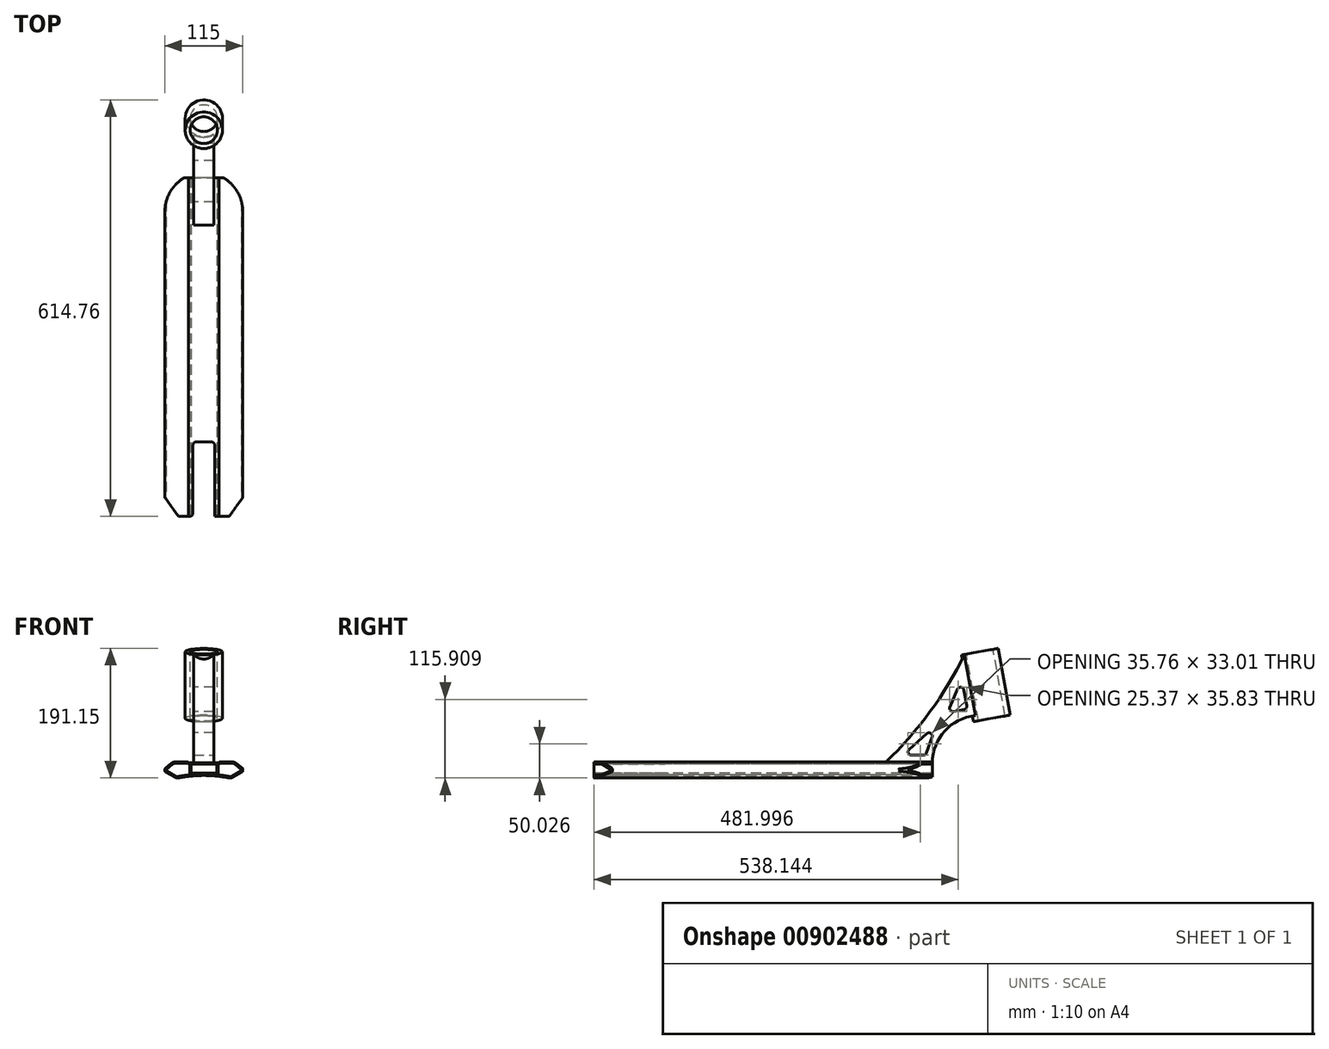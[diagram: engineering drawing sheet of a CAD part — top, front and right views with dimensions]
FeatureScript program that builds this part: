
annotation { "Feature Type Name" : "Feature", "Feature Type Description" : "" }
export const myFeature = defineFeature(function(context is Context, id is Id, definition is map)
    precondition{}
    {
        {
            var Q0;
            Q0=qCreatedBy(makeId("Front.planeOp"),FACE);
            var sketch = newSketch(context, id + "F0", { "sketchPlane" : qUnion([Q0])});
            skLineSegment(sketch, "E0", {"start": v(0, 0) * mm, "end": v(0, 87.82) * mm, "construction": true});
            skLineSegment(sketch, "E1", {"start": v(0, 8.7) * mm, "end": v(-22.5, 8.7) * mm});
            skLineSegment(sketch, "E2", {"start": v(-22.5, 8.7) * mm, "end": v(-22.5, 10) * mm});
            skLineSegment(sketch, "E3", {"start": v(-22.5, 10) * mm, "end": v(-45.58, 10) * mm});
            skLineSegment(sketch, "E4", {"start": v(-45.58, 10) * mm, "end": v(-57.5, 0) * mm});
            skLineSegment(sketch, "E5", {"start": v(-57.5, 0) * mm, "end": v(-57.5, -4) * mm});
            skLineSegment(sketch, "E6", {"start": v(-57.5, -4) * mm, "end": v(-40.18, -14) * mm});
            skLineSegment(sketch, "E7.MirrorCS", {"start": v(22.5, 8.7) * mm, "end": v(22.5, 10) * mm});
            skLineSegment(sketch, "E8.MirrorCS", {"start": v(57.5, 0) * mm, "end": v(57.5, -4) * mm});
            skLineSegment(sketch, "E9.MirrorCS", {"start": v(57.5, -4) * mm, "end": v(40.18, -14) * mm});
            skLineSegment(sketch, "E10.MirrorCS", {"start": v(0, 8.7) * mm, "end": v(22.5, 8.7) * mm});
            skLineSegment(sketch, "E11.MirrorCS", {"start": v(45.58, 10) * mm, "end": v(57.5, 0) * mm});
            skLineSegment(sketch, "E12.MirrorCS", {"start": v(22.5, 10) * mm, "end": v(45.58, 10) * mm});
            skArc(sketch, "E13", {"start": v(40.18, -14) * mm, "mid": v(0, -9.92) * mm, "end": v(-40.18, -14) * mm});
            skSolve(sketch);
        }
        {
            var Q0;
            Q0=makeQuery(id+"F0.imprint","IMPRINT",FACE,{"disambiguationData":[TD([[makeQuery(id+"F0.imprint","IMPRINT",EDGE,{"derivedFrom":sQuery(id+"F0.wireOp",EDGE,"E1")}),1.0]])]});
            extrude(context, id + "F1", {"entities" : qUnion([Q0]), "endBound" : BoundingType.SYMMETRIC, "depth" : 500 * mm, "offsetDistance" : 25 * mm});
        }
        {
            var Q0;
            Q0=qCreatedBy(makeId("Front.planeOp"),FACE);
            var sketch = newSketch(context, id + "F2", { "sketchPlane" : qUnion([Q0])});
            skLineSegment(sketch, "E14.bottom", {"start": v(-19, 6.7) * mm, "end": v(19, 6.7) * mm});
            skLineSegment(sketch, "E14.top", {"start": v(-19, -6.3) * mm, "end": v(19, -6.3) * mm});
            skLineSegment(sketch, "E14.left", {"start": v(-19, 6.7) * mm, "end": v(-19, -6.3) * mm});
            skLineSegment(sketch, "E14.right", {"start": v(19, 6.7) * mm, "end": v(19, -6.3) * mm});
            skSolve(sketch);
        }
        {
            var Q0;
            Q0 = qSketchRegion(id + "F2", true);
            extrude(context, id + "F3", {"entities" : qUnion([Q0]), "operationType" : NewBodyOperationType.REMOVE, "endBound" : BoundingType.SYMMETRIC, "oppositeDirection" : true, "depth" : 500 * mm, "offsetDistance" : 25 * mm});
        }
        {
            var Q0;
            Q0=makeQuery(id+"F1.opExtrude","SWEPT_EDGE",EDGE,{"disambiguationData":[OSD([sQuery(id+"F0.wireOp",EDGE,"E2"),sQuery(id+"F0.wireOp",EDGE,"E3")])]});
            var Q1;
            Q1=makeQuery(id+"F1.opExtrude","SWEPT_EDGE",EDGE,{"disambiguationData":[OSD([sQuery(id+"F0.wireOp",EDGE,"E7.MirrorCS"),sQuery(id+"F0.wireOp",EDGE,"E12.MirrorCS")])]});
            fillet(context, id + "F4", {"entities" : qUnion([Q0, Q1]), "radius" : 2 * mm, "tangentPropagation" : true, "allowEdgeOverflow" : false});
        }
        {
            var Q0;
            Q0=makeQuery(id+"F1.opExtrude","SWEPT_EDGE",EDGE,{"disambiguationData":[OSD([sQuery(id+"F0.wireOp",EDGE,"E3"),sQuery(id+"F0.wireOp",EDGE,"E4")])]});
            var Q1;
            Q1=makeQuery(id+"F1.opExtrude","SWEPT_EDGE",EDGE,{"disambiguationData":[OSD([sQuery(id+"F0.wireOp",EDGE,"E11.MirrorCS"),sQuery(id+"F0.wireOp",EDGE,"E12.MirrorCS")])]});
            var Q2;
            Q2=makeQuery(id+"F1.opExtrude","SWEPT_EDGE",EDGE,{"disambiguationData":[OSD([sQuery(id+"F0.wireOp",EDGE,"E6"),sQuery(id+"F0.wireOp",EDGE,"E13")])]});
            var Q3;
            Q3=makeQuery(id+"F1.opExtrude","SWEPT_EDGE",EDGE,{"disambiguationData":[OSD([sQuery(id+"F0.wireOp",EDGE,"E9.MirrorCS"),sQuery(id+"F0.wireOp",EDGE,"E13")])]});
            fillet(context, id + "F5", {"entities" : qUnion([Q0, Q1, Q2, Q3]), "radius" : 9 * mm, "tangentPropagation" : true, "allowEdgeOverflow" : false});
        }
        {
            var Q0;
            Q0=makeQuery(id+"F1.opExtrude","SWEPT_EDGE",EDGE,{"disambiguationData":[OSD([sQuery(id+"F0.wireOp",EDGE,"E4"),sQuery(id+"F0.wireOp",EDGE,"E5")])]});
            var Q1;
            Q1=makeQuery(id+"F1.opExtrude","SWEPT_EDGE",EDGE,{"disambiguationData":[OSD([sQuery(id+"F0.wireOp",EDGE,"E5"),sQuery(id+"F0.wireOp",EDGE,"E6")])]});
            var Q2;
            Q2=makeQuery(id+"F1.opExtrude","SWEPT_EDGE",EDGE,{"disambiguationData":[OSD([sQuery(id+"F0.wireOp",EDGE,"E8.MirrorCS"),sQuery(id+"F0.wireOp",EDGE,"E11.MirrorCS")])]});
            var Q3;
            Q3=makeQuery(id+"F1.opExtrude","SWEPT_EDGE",EDGE,{"disambiguationData":[OSD([sQuery(id+"F0.wireOp",EDGE,"E8.MirrorCS"),sQuery(id+"F0.wireOp",EDGE,"E9.MirrorCS")])]});
            fillet(context, id + "F6", {"entities" : qUnion([Q0, Q1, Q2, Q3]), "radius" : 1 * mm, "tangentPropagation" : true, "allowEdgeOverflow" : false});
        }
        {
            var Q0;
            Q0=makeQuery(id+"F1.opExtrude","CAP_FACE",FACE,{"disambiguationData":[OSD([sQuery(id+"F0.wireOp",EDGE,"E1"),sQuery(id+"F0.wireOp",EDGE,"E2"),sQuery(id+"F0.wireOp",EDGE,"E3"),sQuery(id+"F0.wireOp",EDGE,"E4"),sQuery(id+"F0.wireOp",EDGE,"E5"),sQuery(id+"F0.wireOp",EDGE,"E6"),sQuery(id+"F0.wireOp",EDGE,"E7.MirrorCS"),sQuery(id+"F0.wireOp",EDGE,"E8.MirrorCS"),sQuery(id+"F0.wireOp",EDGE,"E9.MirrorCS"),sQuery(id+"F0.wireOp",EDGE,"E10.MirrorCS"),sQuery(id+"F0.wireOp",EDGE,"E11.MirrorCS"),sQuery(id+"F0.wireOp",EDGE,"E12.MirrorCS"),sQuery(id+"F0.wireOp",EDGE,"E13")])],"isStart":false});
            var sketch = newSketch(context, id + "F7", { "sketchPlane" : qUnion([Q0])});
            skLineSegment(sketch, "E15.0", {"start": v(-24.37, 8) * mm, "end": v(-42.3, 8) * mm});
            skLineSegment(sketch, "E16.0", {"start": v(-46.8, 6.36) * mm, "end": v(-55.14, -0.63) * mm});
            skArc(sketch, "E17.0", {"start": v(-42.3, 8) * mm, "mid": v(-44.7, 7.58) * mm, "end": v(-46.8, 6.36) * mm});
            skLineSegment(sketch, "E18.0", {"start": v(-55, -3.13) * mm, "end": v(-42.1, -10.58) * mm});
            skArc(sketch, "E19.0", {"start": v(-42.1, -10.58) * mm, "mid": v(-39.78, -11.42) * mm, "end": v(-37.3, -11.4) * mm});
            skLineSegment(sketch, "E20.0", {"start": v(-55.5, -1.4) * mm, "end": v(-55.5, -2.27) * mm});
            skLineSegment(sketch, "E21.0", {"start": v(-24.37, 8) * mm, "end": v(-24.37, 8) * mm});
            skArc(sketch, "E22.0", {"start": v(-21, -9.02) * mm, "mid": v(-29.18, -10.04) * mm, "end": v(-37.3, -11.4) * mm});
            skPoint(sketch, "E23.visualSharp", {"position": v(-55.5, -2.85) * mm});
            skArc(sketch, "E23.filletArc", {"start": v(-55.5, -2.27) * mm, "mid": v(-55.37, -2.77) * mm, "end": v(-55, -3.13) * mm});
            skPoint(sketch, "E24.visualSharp", {"position": v(-55.5, -0.93) * mm});
            skArc(sketch, "E24.filletArc", {"start": v(-55.14, -0.63) * mm, "mid": v(-55.4, -0.98) * mm, "end": v(-55.5, -1.4) * mm});
            skLineSegment(sketch, "E25.0", {"start": v(-21, 6.7) * mm, "end": v(-21, -9.02) * mm});
            skLineSegment(sketch, "E26.0", {"start": v(-22.5, 6.7) * mm, "end": v(-21, 6.7) * mm});
            skArc(sketch, "E27", {"start": v(-22.5, 6.7) * mm, "mid": v(-23.23, 7.64) * mm, "end": v(-24.37, 8) * mm});
            skArc(sketch, "E28.MirrorCS", {"start": v(55.5, -2.27) * mm, "mid": v(55.37, -2.77) * mm, "end": v(55, -3.13) * mm});
            skLineSegment(sketch, "E29.MirrorCS", {"start": v(55.5, -1.4) * mm, "end": v(55.5, -2.27) * mm});
            skArc(sketch, "E30.MirrorCS", {"start": v(55.14, -0.63) * mm, "mid": v(55.4, -0.98) * mm, "end": v(55.5, -1.4) * mm});
            skArc(sketch, "E31.MirrorCS", {"start": v(22.5, 6.7) * mm, "mid": v(23.23, 7.64) * mm, "end": v(24.37, 8) * mm});
            skLineSegment(sketch, "E32.MirrorCS", {"start": v(22.5, 6.7) * mm, "end": v(21, 6.7) * mm});
            skLineSegment(sketch, "E33.MirrorCS", {"start": v(24.37, 8) * mm, "end": v(42.3, 8) * mm});
            skLineSegment(sketch, "E34.MirrorCS", {"start": v(46.8, 6.36) * mm, "end": v(55.14, -0.63) * mm});
            skPoint(sketch, "E35.MirrorP", {"position": v(55.5, -0.93) * mm});
            skArc(sketch, "E36.MirrorCS", {"start": v(42.3, 8) * mm, "mid": v(44.7, 7.58) * mm, "end": v(46.8, 6.36) * mm});
            skLineSegment(sketch, "E37.MirrorCS", {"start": v(24.37, 8) * mm, "end": v(24.37, 8) * mm});
            skPoint(sketch, "E38.MirrorP", {"position": v(55.5, -2.85) * mm});
            skLineSegment(sketch, "E39.MirrorCS", {"start": v(21, 6.7) * mm, "end": v(21, -9.02) * mm});
            skArc(sketch, "E40.MirrorCS", {"start": v(42.1, -10.58) * mm, "mid": v(39.78, -11.42) * mm, "end": v(37.3, -11.4) * mm});
            skArc(sketch, "E41.MirrorCS", {"start": v(21, -9.02) * mm, "mid": v(29.18, -10.04) * mm, "end": v(37.3, -11.4) * mm});
            skLineSegment(sketch, "E42.MirrorCS", {"start": v(55, -3.13) * mm, "end": v(42.1, -10.58) * mm});
            skSolve(sketch);
        }
        {
            var Q0;
            Q0 = qSketchRegion(id + "F7", true);
            extrude(context, id + "F8", {"entities" : qUnion([Q0]), "operationType" : NewBodyOperationType.REMOVE, "endBound" : BoundingType.THROUGH_ALL, "oppositeDirection" : true, "depth" : 25 * mm, "offsetDistance" : 25 * mm});
        }
        {
            var Q0;
            Q0=qCreatedBy(makeId("Top.planeOp"),FACE);
            var sketch = newSketch(context, id + "F9", { "sketchPlane" : qUnion([Q0])});
            skArc(sketch, "E43", {"start": v(57.5, 200) * mm, "mid": v(0, 257.5) * mm, "end": v(-57.5, 200) * mm});
            skLineSegment(sketch, "E44", {"start": v(-57.5, 200) * mm, "end": v(-57.5, 280) * mm});
            skLineSegment(sketch, "E45", {"start": v(57.5, 200) * mm, "end": v(57.5, 280) * mm});
            skLineSegment(sketch, "E46", {"start": v(57.5, 280) * mm, "end": v(-57.5, 280) * mm});
            skSolve(sketch);
        }
        {
            var Q0;
            Q0 = qSketchRegion(id + "F9", true);
            extrude(context, id + "F10", {"entities" : qUnion([Q0]), "operationType" : NewBodyOperationType.REMOVE, "endBound" : BoundingType.THROUGH_ALL, "oppositeDirection" : true, "depth" : 25 * mm, "offsetDistance" : 25 * mm, "hasSecondDirection" : true, "secondDirectionBound" : SecondDirectionBoundingType.THROUGH_ALL, "secondDirectionOppositeDirection" : false, "secondDirectionDepth" : 25 * mm});
        }
        {
            var Q0;
            Q0=qCreatedBy(makeId("Top.planeOp"),FACE);
            var sketch = newSketch(context, id + "F11", { "sketchPlane" : qUnion([Q0])});
            skLineSegment(sketch, "E47", {"start": v(16, -140) * mm, "end": v(-16, -140) * mm});
            skLineSegment(sketch, "E48", {"start": v(-16, -140) * mm, "end": v(-16, -250) * mm});
            skLineSegment(sketch, "E49", {"start": v(-16, -250) * mm, "end": v(-37.49, -250) * mm});
            skLineSegment(sketch, "E50", {"start": v(-37.49, -250) * mm, "end": v(-68, -208) * mm});
            skLineSegment(sketch, "E51", {"start": v(-68, -208) * mm, "end": v(-68, -338) * mm});
            skLineSegment(sketch, "E52", {"start": v(-68, -338) * mm, "end": v(68, -338) * mm});
            skLineSegment(sketch, "E53", {"start": v(68, -338) * mm, "end": v(68, -208) * mm});
            skLineSegment(sketch, "E54", {"start": v(68, -208) * mm, "end": v(37.49, -250) * mm});
            skLineSegment(sketch, "E55", {"start": v(37.49, -250) * mm, "end": v(16, -250) * mm});
            skLineSegment(sketch, "E56", {"start": v(16, -250) * mm, "end": v(16, -140) * mm});
            skSolve(sketch);
        }
        {
            var Q0;
            Q0 = qSketchRegion(id + "F11", true);
            extrude(context, id + "F12", {"entities" : qUnion([Q0]), "operationType" : NewBodyOperationType.REMOVE, "endBound" : BoundingType.THROUGH_ALL, "oppositeDirection" : true, "depth" : 25 * mm, "offsetDistance" : 25 * mm, "hasSecondDirection" : true, "secondDirectionBound" : SecondDirectionBoundingType.THROUGH_ALL, "secondDirectionOppositeDirection" : false, "secondDirectionDepth" : 25 * mm});
        }
        {
            var Q0;
            {var subQ0=sQuery(id+"F11.wireOp",EDGE,"E48");var subQ1=sQuery(id+"F11.wireOp",EDGE,"E47");Q0=makeQuery(id+"F12.boolean.opBoolean","COPY",EDGE,{"disambiguationData":[TD([makeQuery(id+"F3.boolean.opBoolean","COPY",FACE,{"derivedFrom":makeQuery(id+"F3.opExtrude","SWEPT_FACE",FACE,{"disambiguationData":[OSD([sQuery(id+"F2.wireOp",EDGE,"E14.bottom")])]})})])],"derivedFrom":makeQuery(id+"F12.opExtrude","SWEPT_EDGE",EDGE,{"disambiguationData":[OSD([subQ1,subQ0])]})});}
            var Q1;
            {var subQ0=sQuery(id+"F11.wireOp",EDGE,"E47");var subQ1=sQuery(id+"F11.wireOp",EDGE,"E48");Q1=makeQuery(id+"F12.boolean.opBoolean","COPY",EDGE,{"disambiguationData":[TD([makeQuery(id+"F1.opExtrude","SWEPT_FACE",FACE,{"disambiguationData":[OSD([sQuery(id+"F0.wireOp",EDGE,"E13")])]})])],"derivedFrom":makeQuery(id+"F12.opExtrude","SWEPT_EDGE",EDGE,{"disambiguationData":[OSD([subQ0,subQ1])]})});}
            var Q2;
            {var subQ2=sQuery(id+"F11.wireOp",EDGE,"E48");Q2=makeQuery(id+"F12.boolean.opBoolean","COPY",EDGE,{"disambiguationData":[TD([makeQuery(id+"F3.boolean.opBoolean","COPY",FACE,{"derivedFrom":makeQuery(id+"F3.opExtrude","SWEPT_FACE",FACE,{"disambiguationData":[OSD([sQuery(id+"F2.wireOp",EDGE,"E14.bottom")])]})})])],"derivedFrom":makeQuery(id+"F12.opExtrude","SWEPT_EDGE",EDGE,{"disambiguationData":[OSD([subQ2,sQuery(id+"F11.wireOp",EDGE,"E49")])]})});}
            var Q3;
            {var subQ0=sQuery(id+"F0.wireOp",EDGE,"E13");var subQ1=sQuery(id+"F11.wireOp",EDGE,"E48");Q3=makeQuery(id+"F12.boolean.opBoolean","COPY",EDGE,{"disambiguationData":[TD([makeQuery(id+"F1.opExtrude","SWEPT_FACE",FACE,{"disambiguationData":[OSD([subQ0])]})])],"derivedFrom":makeQuery(id+"F12.opExtrude","SWEPT_EDGE",EDGE,{"disambiguationData":[OSD([subQ1,sQuery(id+"F11.wireOp",EDGE,"E49")])]})});}
            var Q4;
            {var subQ0=sQuery(id+"F11.wireOp",EDGE,"E47");var subQ1=sQuery(id+"F11.wireOp",EDGE,"E56");Q4=makeQuery(id+"F12.boolean.opBoolean","COPY",EDGE,{"disambiguationData":[TD([makeQuery(id+"F3.boolean.opBoolean","COPY",FACE,{"derivedFrom":makeQuery(id+"F3.opExtrude","SWEPT_FACE",FACE,{"disambiguationData":[OSD([sQuery(id+"F2.wireOp",EDGE,"E14.bottom")])]})})])],"derivedFrom":makeQuery(id+"F12.opExtrude","SWEPT_EDGE",EDGE,{"disambiguationData":[OSD([subQ0,subQ1])]})});}
            var Q5;
            {var subQ0=sQuery(id+"F11.wireOp",EDGE,"E56");var subQ1=sQuery(id+"F11.wireOp",EDGE,"E47");Q5=makeQuery(id+"F12.boolean.opBoolean","COPY",EDGE,{"disambiguationData":[TD([makeQuery(id+"F1.opExtrude","SWEPT_FACE",FACE,{"disambiguationData":[OSD([sQuery(id+"F0.wireOp",EDGE,"E13")])]})])],"derivedFrom":makeQuery(id+"F12.opExtrude","SWEPT_EDGE",EDGE,{"disambiguationData":[OSD([subQ1,subQ0])]})});}
            var Q6;
            {var subQ2=sQuery(id+"F11.wireOp",EDGE,"E56");Q6=makeQuery(id+"F12.boolean.opBoolean","COPY",EDGE,{"disambiguationData":[TD([makeQuery(id+"F3.boolean.opBoolean","COPY",FACE,{"derivedFrom":makeQuery(id+"F3.opExtrude","SWEPT_FACE",FACE,{"disambiguationData":[OSD([sQuery(id+"F2.wireOp",EDGE,"E14.bottom")])]})})])],"derivedFrom":makeQuery(id+"F12.opExtrude","SWEPT_EDGE",EDGE,{"disambiguationData":[OSD([sQuery(id+"F11.wireOp",EDGE,"E55"),subQ2])]})});}
            var Q7;
            {var subQ0=sQuery(id+"F0.wireOp",EDGE,"E13");var subQ1=sQuery(id+"F11.wireOp",EDGE,"E56");Q7=makeQuery(id+"F12.boolean.opBoolean","COPY",EDGE,{"disambiguationData":[TD([makeQuery(id+"F1.opExtrude","SWEPT_FACE",FACE,{"disambiguationData":[OSD([subQ0])]})])],"derivedFrom":makeQuery(id+"F12.opExtrude","SWEPT_EDGE",EDGE,{"disambiguationData":[OSD([sQuery(id+"F11.wireOp",EDGE,"E55"),subQ1])]})});}
            fillet(context, id + "F13", {"entities" : qUnion([Q0, Q1, Q2, Q3, Q4, Q5, Q6, Q7]), "radius" : 5 * mm, "tangentPropagation" : true, "allowEdgeOverflow" : false});
        }
        {
            var Q0;
            Q0=qCreatedBy(makeId("Right.planeOp"),FACE);
            var sketch = newSketch(context, id + "F14", { "sketchPlane" : qUnion([Q0])});
            skLineSegment(sketch, "E57", {"start": v(180, 8.7) * mm, "end": v(250, 8.7) * mm});
            skArc(sketch, "E58", {"start": v(313.6, 78.4) * mm, "mid": v(268.29, 55.88) * mm, "end": v(250, 8.7) * mm});
            skLineSegment(sketch, "E59", {"start": v(313.6, 78.4) * mm, "end": v(315.06, 70.27) * mm});
            skLineSegment(sketch, "E60", {"start": v(315.06, 70.27) * mm, "end": v(360.34, 78.4) * mm});
            skLineSegment(sketch, "E61", {"start": v(360.34, 78.4) * mm, "end": v(342.66, 176.83) * mm});
            skLineSegment(sketch, "E62", {"start": v(342.66, 176.83) * mm, "end": v(297.38, 168.7) * mm});
            skArc(sketch, "E63", {"start": v(180, 8.7) * mm, "mid": v(245.97, 83.36) * mm, "end": v(297.38, 168.7) * mm});
            skSolve(sketch);
        }
        {
            var Q0;
            Q0 = qSketchRegion(id + "F14", true);
            extrude(context, id + "F15", {"entities" : qUnion([Q0]), "endBound" : BoundingType.SYMMETRIC, "depth" : 30 * mm, "offsetDistance" : 25 * mm});
        }
        {
            var Q0;
            Q0=makeQuery(id+"F15.opExtrude","SWEPT_FACE",FACE,{"disambiguationData":[OSD([sQuery(id+"F14.wireOp",EDGE,"E62")])]});
            var sketch = newSketch(context, id + "F16", { "sketchPlane" : qUnion([Q0])});
            skCircle(sketch, "E64", {"center": v(0, 345.52) * mm, "radius": 27.5 * mm});
            skSolve(sketch);
        }
        {
            var Q0;
            Q0 = qSketchRegion(id + "F16", true);
            var Q1;
            Q1=makeQuery(id+"F15.opExtrude","SWEPT_FACE",FACE,{"disambiguationData":[OSD([sQuery(id+"F14.wireOp",EDGE,"E60")])]});
            extrude(context, id + "F17", {"entities" : qUnion([Q0]), "operationType" : NewBodyOperationType.ADD, "endBound" : BoundingType.UP_TO_SURFACE, "oppositeDirection" : true, "depth" : 25 * mm, "endBoundEntityFace" : qUnion([Q1]), "offsetDistance" : 25 * mm});
        }
        {
            var Q0;
            Q0=makeQuery(id+"F17.boolean.opBoolean","MERGE",FACE,{"derivedFrom":[makeQuery(id+"F15.opExtrude","SWEPT_FACE",FACE,{"disambiguationData":[OSD([sQuery(id+"F14.wireOp",EDGE,"E62")])]}),makeQuery(id+"F17.opExtrude","CAP_FACE",FACE,{"disambiguationData":[OSD([sQuery(id+"F16.wireOp",EDGE,"E64")])],"isStart":true})]});
            var sketch = newSketch(context, id + "F18", { "sketchPlane" : qUnion([Q0])});
            skPoint(sketch, "E65", {"position": v(0, 345.52) * mm});
            skSolve(sketch);
        }
        {
            var Q0;
            Q0=sQuery(id+"F18.wireOp",VERTEX,"E65");
            var Q1;
            Q1=makeQuery(id+"F15.opExtrude","SWEPT_BODY",BODY,{"disambiguationData":[OSD([sQuery(id+"F14.wireOp",EDGE,"E57"),sQuery(id+"F14.wireOp",EDGE,"E58"),sQuery(id+"F14.wireOp",EDGE,"E59"),sQuery(id+"F14.wireOp",EDGE,"E60"),sQuery(id+"F14.wireOp",EDGE,"E61"),sQuery(id+"F14.wireOp",EDGE,"E62"),sQuery(id+"F14.wireOp",EDGE,"E63")])]});
            hole(context, id + "F19", {"style" : HoleStyle.SIMPLE, "endStyle" : HoleEndStyle.THROUGH, "holeDiameter" : 40 * mm, "majorDiameter" : 5 * mm, "isTappedThrough" : true, "tappedDepth" : 12 * mm, "tapClearance" : 3, "locations" : qUnion([Q0]), "scope" : qUnion([Q1])});
        }
        {
            var Q0;
            Q0=makeQuery(id+"F8.boolean.opBoolean","COPY",FACE,{"derivedFrom":makeQuery(id+"F8.opExtrude","SWEPT_FACE",FACE,{"disambiguationData":[OSD([sQuery(id+"F7.wireOp",EDGE,"E39.MirrorCS")])]})});
            var sketch = newSketch(context, id + "F20", { "sketchPlane" : qUnion([Q0])});
            skPoint(sketch, "E66", {"position": v(-236, 0.98) * mm});
            skSolve(sketch);
        }
        {
            var Q0;
            Q0=sQuery(id+"F20.wireOp",VERTEX,"E66");
            var Q1;
            Q1=makeQuery(id+"F15.opExtrude","SWEPT_BODY",BODY,{"disambiguationData":[OSD([sQuery(id+"F14.wireOp",EDGE,"E57"),sQuery(id+"F14.wireOp",EDGE,"E58"),sQuery(id+"F14.wireOp",EDGE,"E59"),sQuery(id+"F14.wireOp",EDGE,"E60"),sQuery(id+"F14.wireOp",EDGE,"E61"),sQuery(id+"F14.wireOp",EDGE,"E62"),sQuery(id+"F14.wireOp",EDGE,"E63")])]});
            hole(context, id + "F21", {"style" : HoleStyle.SIMPLE, "endStyle" : HoleEndStyle.THROUGH, "holeDiameter" : 8 * mm, "majorDiameter" : 5 * mm, "isTappedThrough" : true, "tappedDepth" : 12 * mm, "tapClearance" : 3, "locations" : qUnion([Q0]), "scope" : qUnion([Q1])});
        }
        {
            var Q0;
            Q0=makeQuery(id+"F15.opExtrude","CAP_FACE",FACE,{"disambiguationData":[OSD([sQuery(id+"F14.wireOp",EDGE,"E57"),sQuery(id+"F14.wireOp",EDGE,"E58"),sQuery(id+"F14.wireOp",EDGE,"E59"),sQuery(id+"F14.wireOp",EDGE,"E60"),sQuery(id+"F14.wireOp",EDGE,"E61"),sQuery(id+"F14.wireOp",EDGE,"E62"),sQuery(id+"F14.wireOp",EDGE,"E63")])],"isStart":false});
            var sketch = newSketch(context, id + "F22", { "sketchPlane" : qUnion([Q0])});
            skLineSegment(sketch, "E67", {"start": v(293.68, 132.47) * mm, "end": v(301.63, 88.18) * mm});
            skLineSegment(sketch, "E68", {"start": v(301.63, 88.18) * mm, "end": v(272.1, 82.88) * mm});
            skLineSegment(sketch, "E69", {"start": v(272.1, 82.88) * mm, "end": v(293.68, 132.47) * mm});
            skPoint(sketch, "E70.endSnap0", {"position": v(245.94, 83.33) * mm});
            skLineSegment(sketch, "E71", {"start": v(240, 20) * mm, "end": v(206, 20) * mm});
            skLineSegment(sketch, "E72", {"start": v(206, 20) * mm, "end": v(256.38, 65) * mm});
            skLineSegment(sketch, "E73", {"start": v(256.38, 65) * mm, "end": v(240, 20) * mm});
            skSolve(sketch);
        }
        {
            var Q0;
            Q0 = qSketchRegion(id + "F22", true);
            extrude(context, id + "F23", {"entities" : qUnion([Q0]), "operationType" : NewBodyOperationType.REMOVE, "endBound" : BoundingType.THROUGH_ALL, "oppositeDirection" : true, "depth" : 25 * mm, "offsetDistance" : 25 * mm});
        }
        {
            var Q0;
            Q0=makeQuery(id+"F23.boolean.opBoolean","COPY",EDGE,{"derivedFrom":makeQuery(id+"F23.opExtrude","SWEPT_EDGE",EDGE,{"disambiguationData":[OSD([sQuery(id+"F22.wireOp",EDGE,"E67"),sQuery(id+"F22.wireOp",EDGE,"E69")])]})});
            var Q1;
            Q1=makeQuery(id+"F23.boolean.opBoolean","COPY",EDGE,{"derivedFrom":makeQuery(id+"F23.opExtrude","SWEPT_EDGE",EDGE,{"disambiguationData":[OSD([sQuery(id+"F22.wireOp",EDGE,"E67"),sQuery(id+"F22.wireOp",EDGE,"E68")])]})});
            var Q2;
            Q2=makeQuery(id+"F23.boolean.opBoolean","COPY",EDGE,{"derivedFrom":makeQuery(id+"F23.opExtrude","SWEPT_EDGE",EDGE,{"disambiguationData":[OSD([sQuery(id+"F22.wireOp",EDGE,"E68"),sQuery(id+"F22.wireOp",EDGE,"E69")])]})});
            var Q3;
            Q3=makeQuery(id+"F23.boolean.opBoolean","COPY",EDGE,{"derivedFrom":makeQuery(id+"F23.opExtrude","SWEPT_EDGE",EDGE,{"disambiguationData":[OSD([sQuery(id+"F22.wireOp",EDGE,"E71"),sQuery(id+"F22.wireOp",EDGE,"E73")])]})});
            var Q4;
            Q4=makeQuery(id+"F23.boolean.opBoolean","COPY",EDGE,{"derivedFrom":makeQuery(id+"F23.opExtrude","SWEPT_EDGE",EDGE,{"disambiguationData":[OSD([sQuery(id+"F22.wireOp",EDGE,"E72"),sQuery(id+"F22.wireOp",EDGE,"E73")])]})});
            var Q5;
            Q5=makeQuery(id+"F23.boolean.opBoolean","COPY",EDGE,{"derivedFrom":makeQuery(id+"F23.opExtrude","SWEPT_EDGE",EDGE,{"disambiguationData":[OSD([sQuery(id+"F22.wireOp",EDGE,"E71"),sQuery(id+"F22.wireOp",EDGE,"E72")])]})});
            fillet(context, id + "F24", {"entities" : qUnion([Q0, Q1, Q2, Q3, Q4, Q5]), "radius" : 5 * mm, "tangentPropagation" : true, "allowEdgeOverflow" : false});
        }
    });
